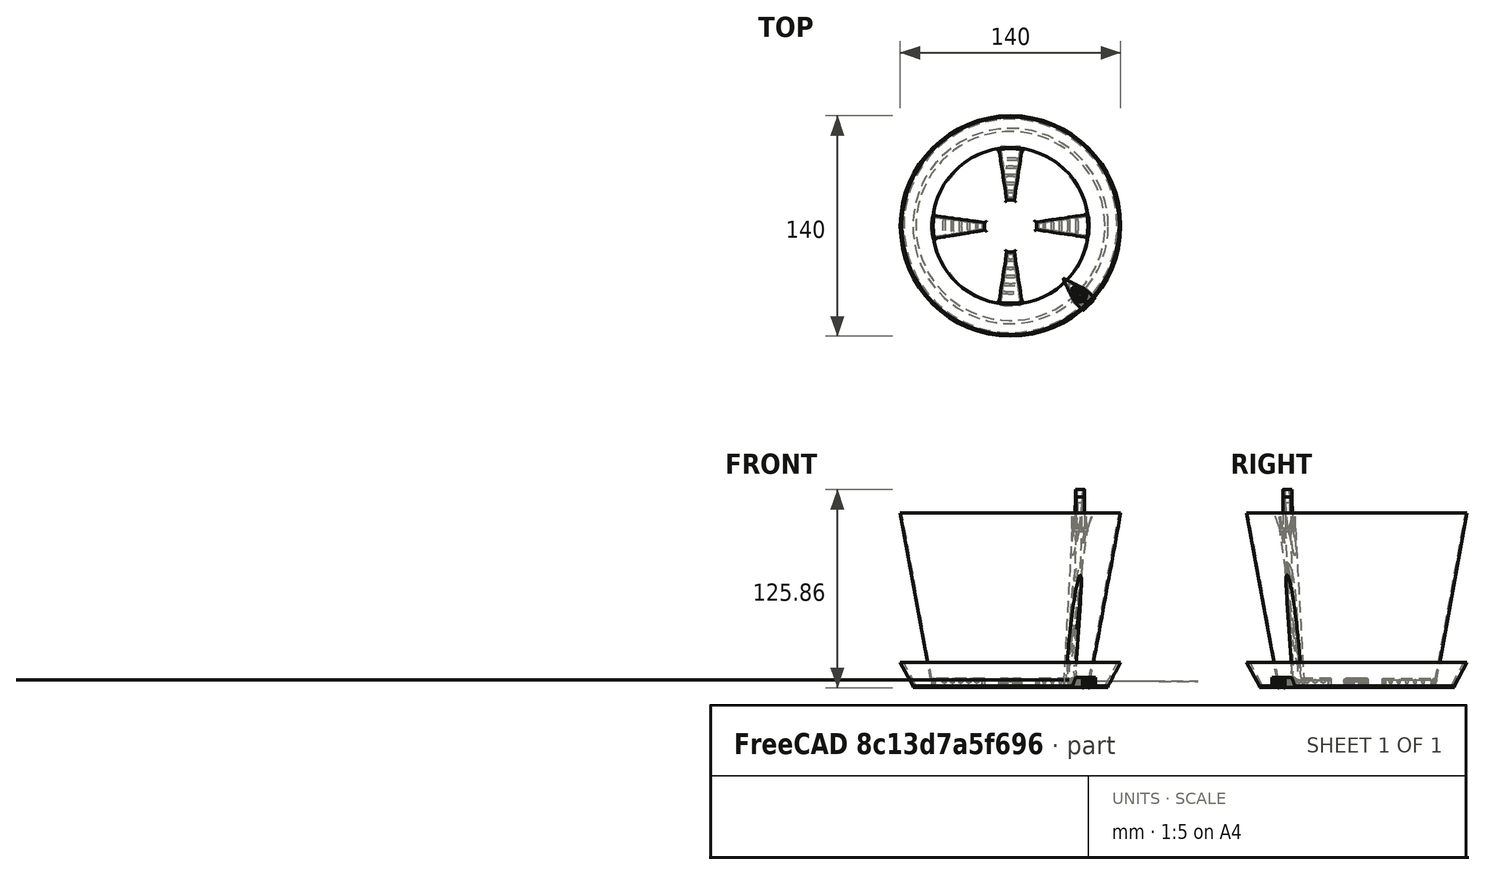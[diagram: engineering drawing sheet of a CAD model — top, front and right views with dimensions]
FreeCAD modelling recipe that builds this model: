
FCSTD DOCUMENT  (FreeCAD 0.19R19056 (Git))
Label: undervase3
License: All rights reserved
LicenseURL: http://en.wikipedia.org/wiki/All_rights_reserved
objects: Sketcher::SketchObject×32, PartDesign::Pad×9, PartDesign::AdditiveLoft×6, PartDesign::Pocket×6, PartDesign::Fillet×2, PartDesign::Body×2, PartDesign::SubtractivePipe×2, PartDesign::Chamfer×1, PartDesign::Thickness×1, PartDesign::AdditivePipe×1, PartDesign::Groove×1
note: 88 computed .brp shape members not serialized (recipe doc carries the construction recipe); baked Part::Feature solids carry a one-line shape summary decoded from their .brp

FEATURE [Sketcher::SketchObject] Sketch
  MapMode = 5
  Support = -> [XY_Plane]
  sketch-geometry (1):
    g0: Circle CenterX=0 CenterY=0 CenterZ=0 NormalX=0 NormalY=0 NormalZ=1 AngleXU=0 Radius=62
  constraints (2):
    c: Coincident(g0,g-1)
    c: Radius(g0) = 62
FEATURE [PartDesign::Pad] Pad
  Length = 1.6
  Length2 = 100
  Profile = -> Sketch
  Type = 0
FEATURE [Sketcher::SketchObject] Sketch001
  MapMode = 5
  Placement = pos=(0,0,1.6) rot=(0,0,1;0rad)
  Support = -> [Pad]
  sketch-geometry (2):
    g0: Circle CenterX=0 CenterY=0 CenterZ=0 NormalX=0 NormalY=0 NormalZ=1 AngleXU=0 Radius=60
    g1: Circle CenterX=0 CenterY=0 CenterZ=0 NormalX=0 NormalY=0 NormalZ=1 AngleXU=0 Radius=62
  constraints (4):
    c: Coincident(g0,g-1)
    c: Coincident(g1,g0)
    c: Radius(g0) = 60
    c: Radius(g1) = 62
FEATURE [Sketcher::SketchObject] Sketch002
  AttachmentOffset = pos=(0,0,15) rot=(0,0,1;0rad)
  MapMode = 5
  Placement = pos=(0,0,16.6) rot=(0,0,1;0rad)
  Support = -> [Pad]
  sketch-geometry (2):
    g0: Circle CenterX=0 CenterY=0 CenterZ=0 NormalX=0 NormalY=0 NormalZ=1 AngleXU=0 Radius=68
    g1: Circle CenterX=0 CenterY=0 CenterZ=0 NormalX=0 NormalY=0 NormalZ=1 AngleXU=0 Radius=70
  constraints (4):
    c: Coincident(g0,g-1)
    c: Coincident(g1,g0)
    c: Radius(g1) = 70
    c: Radius(g0) = 68
FEATURE [PartDesign::AdditiveLoft] AdditiveLoft
  BaseFeature = -> Pad
  Closed = false
  Profile = -> Sketch001
  Ruled = false
  Sections = -> [Sketch002]
FEATURE [PartDesign::Chamfer] Chamfer
  Base = -> AdditiveLoft [Edge6]
  BaseFeature = -> AdditiveLoft
  Size = 0.5
FEATURE [Sketcher::SketchObject] Sketch018
  MapMode = 5
  Placement = pos=(0,0,1.6) rot=(0,0,1;0rad)
  sketch-geometry (2):
    g0: Circle CenterX=0 CenterY=0 CenterZ=0 NormalX=0 NormalY=0 NormalZ=1 AngleXU=0 Radius=50
    g1: Circle CenterX=0 CenterY=0 CenterZ=0 NormalX=0 NormalY=0 NormalZ=1 AngleXU=0 Radius=49.1
  constraints (4):
    c: Coincident(g0,g-1)
    c: Radius(g0) = 50
    c: Coincident(g1,g0)
    c: Radius(g1) = 49.1
FEATURE [Sketcher::SketchObject] Sketch019
  AttachmentOffset = pos=(0,0,110) rot=(0,0,1;0rad)
  MapMode = 5
  Placement = pos=(0,0,111.6) rot=(0,0,1;0rad)
  sketch-geometry (2):
    g0: Circle CenterX=0 CenterY=0 CenterZ=0 NormalX=0 NormalY=0 NormalZ=1 AngleXU=0 Radius=70
    g1: Circle CenterX=0 CenterY=0 CenterZ=0 NormalX=0 NormalY=0 NormalZ=1 AngleXU=0 Radius=69.1
  constraints (4):
    c: Coincident(g0,g-1)
    c: Coincident(g1,g0)
    c: Radius(g1) = 69.1
    c: Radius(g0) = 70
FEATURE [PartDesign::AdditiveLoft] AdditiveLoft001
  BaseFeature = -> Chamfer
  Closed = false
  Profile = -> Sketch018
  Ruled = false
  Sections = -> [Sketch019]
FEATURE [Sketcher::SketchObject] Sketch021
  AttachmentOffset = pos=(0,0,-50) rot=(0,0,1;0rad)
  MapMode = 5
  Placement = pos=(0,0,51.6) rot=(1,0,0;3.14159rad)
  sketch-geometry (2):
    g0: Circle CenterX=0 CenterY=0 CenterZ=0 NormalX=0 NormalY=0 NormalZ=1 AngleXU=0 Radius=2
    g1: Circle CenterX=0 CenterY=0 CenterZ=0 NormalX=0 NormalY=0 NormalZ=1 AngleXU=0 Radius=3
  constraints (4):
    c: Coincident(g0,g-1)
    c: Coincident(g1,g0)
    c: Radius(g1) = 3
    c: Radius(g0) = 2
FEATURE [Sketcher::SketchObject] Sketch022
  AttachmentOffset = pos=(0,0,-100) rot=(0,0,1;0rad)
  MapMode = 5
  Placement = pos=(0,0,101.6) rot=(1,0,0;3.14159rad)
  sketch-geometry (2):
    g0: Circle CenterX=0 CenterY=0 CenterZ=0 NormalX=0 NormalY=0 NormalZ=1 AngleXU=0 Radius=2
    g1: Circle CenterX=0 CenterY=0 CenterZ=0 NormalX=0 NormalY=0 NormalZ=1 AngleXU=0 Radius=2.8
  constraints (4):
    c: Coincident(g0,g-1)
    c: Coincident(g1,g0)
    c: Radius(g0) = 2
    c: Radius(g1) = 2.8
FEATURE [PartDesign::AdditiveLoft] AdditiveLoft002
  BaseFeature = -> AdditiveLoft001
  Closed = false
  Profile = -> Sketch021
  Ruled = false
  Sections = -> [Sketch022]
FEATURE [Sketcher::SketchObject] Sketch026
  ExternalGeometry = -> [Sketch018]
  MapMode = 5
  Placement = pos=(0,0,1) rot=(1,0,0;3.14159rad)
  sketch-geometry (59):
    g0: LineSegment [constr] StartX=0 StartY=0 StartZ=0 EndX=-7.39047 EndY=-49.4508 EndZ=0
    g1: LineSegment [constr] StartX=7.39047 StartY=-49.4508 StartZ=0 EndX=-9e-16 EndY=0 EndZ=0
    g2: LineSegment [constr] StartX=49.4508 StartY=-7.39047 StartZ=0 EndX=0 EndY=0 EndZ=0
    g3: LineSegment [constr] StartX=49.4508 StartY=7.39047 StartZ=0 EndX=0 EndY=0 EndZ=0
    g4: LineSegment [constr] StartX=7.39047 StartY=49.4508 StartZ=0 EndX=9e-16 EndY=0 EndZ=0
    g5: LineSegment [constr] StartX=-7.39047 StartY=49.4508 StartZ=0 EndX=0 EndY=0 EndZ=0
    g6: Circle [constr] CenterX=0 CenterY=0 CenterZ=0 NormalX=0 NormalY=0 NormalZ=1 AngleXU=0 Radius=7
    g7: LineSegment [constr] StartX=-49.5634 StartY=-6.59349 StartZ=0 EndX=0 EndY=0 EndZ=0
    g8: LineSegment [constr] StartX=-49.3254 StartY=8.18553 StartZ=0 EndX=0 EndY=0 EndZ=0
    g9: LineSegment [constr] StartX=6.40003 StartY=-49.5887 StartZ=0 EndX=-9e-16 EndY=-6.92311 EndZ=0
    g10: LineSegment [constr] StartX=-6.40003 StartY=-49.5887 StartZ=0 EndX=-9e-16 EndY=-6.92311 EndZ=0
    g11: LineSegment [constr] StartX=49.5887 StartY=6.40003 StartZ=0 EndX=6.92311 EndY=0 EndZ=0
    g12: LineSegment [constr] StartX=49.5887 StartY=-6.40003 StartZ=0 EndX=6.92311 EndY=0 EndZ=0
    g13: LineSegment [constr] StartX=-6.40004 StartY=49.5887 StartZ=0 EndX=0 EndY=6.92311 EndZ=0
    g14: LineSegment [constr] StartX=6.40003 StartY=49.5887 StartZ=0 EndX=0 EndY=6.92311 EndZ=0
    g15: Circle [constr] CenterX=0 CenterY=0 CenterZ=0 NormalX=0 NormalY=0 NormalZ=1 AngleXU=0 Radius=16.5
    g16: LineSegment [constr] StartX=-49.4793 StartY=7.19744 StartZ=0 EndX=-6.92221 EndY=0.111443 EndZ=0
    g17: LineSegment [constr] StartX=-49.6853 StartY=-5.60096 StartZ=0 EndX=-6.92221 EndY=0.111443 EndZ=0
    g18: GeomPoint X=-1.03467 Y=6.92311 Z=0
    g19: GeomPoint X=1.03467 Y=6.92311 Z=0
    g20: GeomPoint X=6.92311 Y=1.03467 Z=0
    g21: GeomPoint X=6.92311 Y=-1.03467 Z=0
    g22: GeomPoint X=1.03467 Y=-6.92311 Z=0
    g23: GeomPoint X=-1.03467 Y=-6.92311 Z=0
    g24: GeomPoint X=-6.93887 Y=-0.923089 Z=0
    g25: GeomPoint X=-6.90556 Y=1.14597 Z=0
    g26: ArcOfCircle CenterX=0 CenterY=0 CenterZ=0 NormalX=0 NormalY=0 NormalZ=1 AngleXU=0 Radius=50 StartAngle=2.97714 EndAngle=2.99714
    g27: ArcOfCircle CenterX=0 CenterY=0 CenterZ=0 NormalX=0 NormalY=0 NormalZ=1 AngleXU=0 Radius=50 StartAngle=3.25385 EndAngle=3.27385
    g28: ArcOfCircle CenterX=0 CenterY=0 CenterZ=0 NormalX=0 NormalY=0 NormalZ=1 AngleXU=0 Radius=50 StartAngle=0.128353 EndAngle=0.148353
    g29: ArcOfCircle CenterX=0 CenterY=0 CenterZ=0 NormalX=0 NormalY=0 NormalZ=1 AngleXU=0 Radius=50 StartAngle=6.13483 EndAngle=6.15483
    g30: ArcOfCircle CenterX=0 CenterY=0 CenterZ=0 NormalX=0 NormalY=0 NormalZ=1 AngleXU=0 Radius=50 StartAngle=4.56404 EndAngle=4.58404
    g31: ArcOfCircle CenterX=0 CenterY=0 CenterZ=0 NormalX=0 NormalY=0 NormalZ=1 AngleXU=0 Radius=50 StartAngle=4.84074 EndAngle=4.86074
    g32: ArcOfCircle CenterX=0 CenterY=0 CenterZ=0 NormalX=0 NormalY=0 NormalZ=1 AngleXU=0 Radius=50 StartAngle=1.69915 EndAngle=1.71915
    g33: ArcOfCircle CenterX=0 CenterY=0 CenterZ=0 NormalX=0 NormalY=0 NormalZ=1 AngleXU=0 Radius=50 StartAngle=1.42244 EndAngle=1.44244
    g34: Circle [constr] CenterX=0 CenterY=0 CenterZ=0 NormalX=0 NormalY=0 NormalZ=1 AngleXU=0 Radius=18
    g35: LineSegment StartX=-49.3254 StartY=8.18553 StartZ=0 EndX=-16.2774 EndY=2.70123 EndZ=0
    g36: LineSegment StartX=-49.4793 StartY=7.19744 StartZ=0 EndX=-17.8953 EndY=1.93853 EndZ=0
    g37: LineSegment StartX=-49.6853 StartY=-5.60096 StartZ=0 EndX=-17.9484 EndY=-1.36147 EndZ=0
    g38: LineSegment StartX=-49.5634 StartY=-6.59349 StartZ=0 EndX=-16.3559 EndY=-2.17585 EndZ=0
    g39: LineSegment StartX=49.4508 StartY=7.39047 StartZ=0 EndX=16.3188 EndY=2.43886 EndZ=0
    g40: LineSegment StartX=49.5887 StartY=6.40003 StartZ=0 EndX=17.9242 EndY=1.65021 EndZ=0
    g41: LineSegment StartX=49.5887 StartY=-6.40003 StartZ=0 EndX=17.9242 EndY=-1.65021 EndZ=0
    g42: LineSegment StartX=49.4508 StartY=-7.39047 StartZ=0 EndX=16.3188 EndY=-2.43886 EndZ=0
    g43: ArcOfCircle CenterX=0 CenterY=0 CenterZ=0 NormalX=0 NormalY=0 NormalZ=1 AngleXU=0 Radius=18 StartAngle=3.03369 EndAngle=3.2173
    g44: ArcOfCircle CenterX=0 CenterY=0 CenterZ=0 NormalX=0 NormalY=0 NormalZ=1 AngleXU=0 Radius=16.5 StartAngle=2.97714 EndAngle=3.27385
    g45: ArcOfCircle CenterX=0 CenterY=0 CenterZ=0 NormalX=0 NormalY=0 NormalZ=1 AngleXU=0 Radius=18 StartAngle=6.19138 EndAngle=6.37499
    g46: ArcOfCircle CenterX=0 CenterY=0 CenterZ=0 NormalX=0 NormalY=0 NormalZ=1 AngleXU=0 Radius=16.5 StartAngle=6.13483 EndAngle=6.43154
    g47: LineSegment StartX=-7.39047 StartY=49.4508 StartZ=0 EndX=-2.43886 EndY=16.3188 EndZ=0
    g48: LineSegment StartX=-6.40004 StartY=49.5887 StartZ=0 EndX=-1.65022 EndY=17.9242 EndZ=0
    g49: LineSegment StartX=6.40003 StartY=49.5887 StartZ=0 EndX=1.65021 EndY=17.9242 EndZ=0
    g50: LineSegment StartX=7.39047 StartY=49.4508 StartZ=0 EndX=2.43886 EndY=16.3188 EndZ=0
    g51: ArcOfCircle CenterX=0 CenterY=0 CenterZ=0 NormalX=0 NormalY=0 NormalZ=1 AngleXU=0 Radius=16.5 StartAngle=1.42244 EndAngle=1.71915
    g52: ArcOfCircle CenterX=0 CenterY=0 CenterZ=0 NormalX=0 NormalY=0 NormalZ=1 AngleXU=0 Radius=18 StartAngle=1.47899 EndAngle=1.6626
    g53: LineSegment StartX=-7.39047 StartY=-49.4508 StartZ=0 EndX=-2.43886 EndY=-16.3188 EndZ=0
    g54: LineSegment StartX=-6.40003 StartY=-49.5887 StartZ=0 EndX=-1.65021 EndY=-17.9242 EndZ=0
    g55: LineSegment StartX=6.40003 StartY=-49.5887 StartZ=0 EndX=1.65021 EndY=-17.9242 EndZ=0
    g56: LineSegment StartX=7.39047 StartY=-49.4508 StartZ=0 EndX=2.43886 EndY=-16.3188 EndZ=0
    g57: ArcOfCircle CenterX=0 CenterY=0 CenterZ=0 NormalX=0 NormalY=0 NormalZ=1 AngleXU=0 Radius=16.5 StartAngle=4.56404 EndAngle=4.86074
    g58: ArcOfCircle CenterX=0 CenterY=0 CenterZ=0 NormalX=0 NormalY=0 NormalZ=1 AngleXU=0 Radius=18 StartAngle=4.62058 EndAngle=4.8042
  constraints (148):
    c: Coincident(g8,g7)
    c: Radius(g6) = 7
    c: Coincident(g10,g9)
    c: Coincident(g12,g11)
    c: Coincident(g14,g13)
    c: Radius(g15) = 16.5
    c: Coincident(g6,g-1)
    c: Coincident(g15,g-1)
    c: PointOnObject(g11,g-3)
    c: PointOnObject(g12,g-3)
    c: PointOnObject(g4,g-3)
    c: PointOnObject(g5,g-3)
    c: PointOnObject(g8,g-3)
    c: PointOnObject(g7,g-3)
    c: PointOnObject(g10,g-3)
    c: PointOnObject(g1,g-3)
    c: Coincident(g4,g-1)
    c: Coincident(g0,g-1)
    c: Coincident(g7,g1)
    c: Coincident(g7,g-1)
    c: Coincident(g2,g-1)
    c: Coincident(g3,g-1)
    c: Coincident(g5,g-1)
    c: Coincident(g17,g16)
    c: Angle(g8,g7) = 0.296706
    c: Angle(g4,g5) = 0.296706
    c: Angle(g2,g3) = 0.296706
    c: Angle(g0,g1) = 0.296706
    c: PointOnObject(g18,g6)
    c: PointOnObject(g19,g6)
    c: PointOnObject(g20,g6)
    c: PointOnObject(g21,g6)
    c: PointOnObject(g22,g6)
    c: PointOnObject(g24,g6)
    c: PointOnObject(g25,g6)
    c: PointOnObject(g25,g8)
    c: PointOnObject(g24,g7)
    c: PointOnObject(g23,g0)
    c: PointOnObject(g22,g1)
    c: PointOnObject(g21,g2)
    c: PointOnObject(g20,g3)
    c: PointOnObject(g19,g4)
    c: PointOnObject(g18,g5)
    c: PointOnObject(g23,g6)
    c: Symmetric(g23,g22,g9)
    c: Symmetric(g25,g24,g16)
    c: Symmetric(g18,g19,g13)
    c: Symmetric(g20,g21,g11)
    c: PointOnObject(g13,g-2)
    c: PointOnObject(g11,g-1)
    c: PointOnObject(g9,g-2)
    c: Distance(g0,g10) = 1
    c: Distance(g11,g3) = 1
    c: Distance(g4,g14) = 1
    c: Distance(g8,g16) = 1
    c: Distance(g17,g7) = 1
    c: Coincident(g26,g-1)
    c: Coincident(g26,g8)
    c: Coincident(g26,g16)
    c: Coincident(g27,g26)
    c: Coincident(g27,g17)
    c: Coincident(g27,g7)
    c: Coincident(g28,g26)
    c: Coincident(g28,g3)
    c: Coincident(g28,g11)
    c: Coincident(g29,g26)
    c: Coincident(g29,g12)
    c: Coincident(g29,g2)
    c: Distance(g29,g29) = 1
    c: Coincident(g30,g26)
    c: Coincident(g30,g0)
    c: Coincident(g30,g10)
    c: Coincident(g31,g26)
    c: Coincident(g31,g9)
    c: Coincident(g31,g1)
    c: Coincident(g32,g26)
    c: Coincident(g32,g5)
    c: Coincident(g32,g13)
    c: Coincident(g33,g26)
    c: Coincident(g33,g14)
    c: Coincident(g33,g4)
    c: Coincident(g34,g26)
    c: Radius(g34) = 18
    c: Coincident(g35,g26)
    c: PointOnObject(g35,g8)
    c: Coincident(g36,g26)
    c: PointOnObject(g36,g16)
    c: Coincident(g37,g27)
    c: PointOnObject(g37,g17)
    c: Coincident(g38,g27)
    c: PointOnObject(g38,g7)
    c: Coincident(g39,g28)
    c: PointOnObject(g39,g3)
    c: Coincident(g40,g28)
    c: PointOnObject(g40,g11)
    c: Coincident(g41,g29)
    c: PointOnObject(g41,g12)
    c: Coincident(g42,g29)
    c: PointOnObject(g42,g2)
    c: PointOnObject(g36,g34)
    c: PointOnObject(g35,g15)
    c: PointOnObject(g41,g34)
    c: PointOnObject(g39,g15)
    c: Coincident(g43,g26)
    c: Coincident(g43,g36)
    c: Coincident(g43,g37)
    c: Coincident(g44,g26)
    c: Coincident(g44,g35)
    c: Coincident(g44,g38)
    c: Coincident(g45,g26)
    c: Coincident(g45,g40)
    c: Coincident(g45,g41)
    c: Coincident(g46,g26)
    c: Coincident(g46,g39)
    c: Coincident(g46,g42)
    c: Coincident(g47,g32)
    c: PointOnObject(g47,g5)
    c: Coincident(g48,g32)
    c: PointOnObject(g48,g13)
    c: Coincident(g49,g33)
    c: PointOnObject(g49,g14)
    c: Coincident(g50,g33)
    c: PointOnObject(g50,g4)
    c: PointOnObject(g47,g15)
    c: PointOnObject(g49,g34)
    c: Coincident(g51,g26)
    c: Coincident(g51,g47)
    c: Coincident(g51,g50)
    c: Coincident(g52,g26)
    c: Coincident(g52,g48)
    c: Coincident(g52,g49)
    c: Coincident(g53,g30)
    c: PointOnObject(g53,g0)
    c: Coincident(g54,g30)
    c: PointOnObject(g54,g10)
    c: Coincident(g55,g31)
    c: PointOnObject(g55,g9)
    c: Coincident(g56,g31)
    c: PointOnObject(g56,g1)
    c: PointOnObject(g56,g15)
    c: PointOnObject(g54,g34)
    c: PointOnObject(g55,g34)
    c: Coincident(g57,g26)
    c: Coincident(g57,g53)
    c: Coincident(g57,g56)
    c: Coincident(g58,g26)
    c: Coincident(g58,g54)
    c: Coincident(g58,g55)
FEATURE [PartDesign::Pad] Pad017
  BaseFeature = -> AdditiveLoft002
  Length = 4
  Length2 = 100
  Profile = -> Sketch026
  Reversed = true
  Type = 0
FEATURE [Sketcher::SketchObject] Sketch027
  AttachmentOffset = pos=(0,0,51) rot=(0,0,1;0rad)
  ExternalGeometry = -> [Pad017]
  MapMode = 5
  Placement = pos=(0,-51,-5.2771e-12) rot=(1,0,0;1.5708rad)
  Support = -> [XZ_Plane]
  sketch-geometry (4):
    g0: LineSegment StartX=-6.35823 StartY=5 StartZ=0 EndX=6.26649 EndY=5 EndZ=0
    g1: LineSegment StartX=6.26649 StartY=5 StartZ=0 EndX=6.26649 EndY=1.6 EndZ=0
    g2: LineSegment StartX=6.26649 StartY=1.6 StartZ=0 EndX=-6.35823 EndY=1.6 EndZ=0
    g3: LineSegment StartX=-6.35823 StartY=1.6 StartZ=0 EndX=-6.35823 EndY=5 EndZ=0
  constraints (10):
    c: Coincident(g0,g1)
    c: Coincident(g1,g2)
    c: Coincident(g2,g3)
    c: Coincident(g3,g0)
    c: Horizontal(g0)
    c: Horizontal(g2)
    c: Vertical(g1)
    c: Vertical(g3)
    c: Coincident(g0,g-3)
    c: Coincident(g1,g-4)
FEATURE [PartDesign::Pocket] Pocket
  BaseFeature = -> Pad017
  Length = 4
  Length2 = 100
  Profile = -> Sketch027
  Type = 0
FEATURE [Sketcher::SketchObject] Sketch028
  AttachmentOffset = pos=(0,0,-50.5) rot=(0,0,1;0rad)
  ExternalGeometry = -> [Pocket]
  MapMode = 5
  Placement = pos=(0,50.5,5.2254e-12) rot=(1,0,0;1.5708rad)
  Support = -> [XZ_Plane]
  sketch-geometry (4):
    g0: LineSegment StartX=-6.35823 StartY=5 StartZ=0 EndX=6.26649 EndY=5 EndZ=0
    g1: LineSegment StartX=6.26649 StartY=5 StartZ=0 EndX=6.26649 EndY=1.6 EndZ=0
    g2: LineSegment StartX=6.26649 StartY=1.6 StartZ=0 EndX=-6.35823 EndY=1.6 EndZ=0
    g3: LineSegment StartX=-6.35823 StartY=1.6 StartZ=0 EndX=-6.35823 EndY=5 EndZ=0
  constraints (10):
    c: Coincident(g0,g1)
    c: Coincident(g1,g2)
    c: Coincident(g2,g3)
    c: Coincident(g3,g0)
    c: Horizontal(g0)
    c: Horizontal(g2)
    c: Vertical(g1)
    c: Vertical(g3)
    c: Coincident(g0,g-4)
    c: Coincident(g1,g-3)
FEATURE [PartDesign::Pocket] Pocket001
  BaseFeature = -> Pocket
  Length = 3
  Length2 = 100
  Profile = -> Sketch028
  Reversed = true
  Type = 0
FEATURE [Sketcher::SketchObject] Sketch029
  AttachmentOffset = pos=(0,0,50.5) rot=(0,0,1;0rad)
  ExternalGeometry = -> [Pocket001]
  MapMode = 5
  Placement = pos=(50.5,-5.7019e-12,5.7019e-12) rot=(0.57735,0.57735,0.57735;2.0944rad)
  Support = -> [YZ_Plane]
  sketch-geometry (4):
    g0: LineSegment StartX=-6.35821 StartY=5 StartZ=0 EndX=6.26649 EndY=5 EndZ=0
    g1: LineSegment StartX=6.26649 StartY=5 StartZ=0 EndX=6.26649 EndY=1.6 EndZ=0
    g2: LineSegment StartX=6.26649 StartY=1.6 StartZ=0 EndX=-6.35821 EndY=1.6 EndZ=0
    g3: LineSegment StartX=-6.35821 StartY=1.6 StartZ=0 EndX=-6.35821 EndY=5 EndZ=0
  constraints (10):
    c: Coincident(g0,g1)
    c: Coincident(g1,g2)
    c: Coincident(g2,g3)
    c: Coincident(g3,g0)
    c: Horizontal(g0)
    c: Horizontal(g2)
    c: Vertical(g1)
    c: Vertical(g3)
    c: Coincident(g0,g-3)
    c: Coincident(g1,g-4)
FEATURE [PartDesign::Pocket] Pocket002
  BaseFeature = -> Pocket001
  Length = 3
  Length2 = 100
  Profile = -> Sketch029
  Type = 0
FEATURE [Sketcher::SketchObject] Sketch030
  AttachmentOffset = pos=(0,0,-50.5) rot=(0,0,1;0rad)
  ExternalGeometry = -> [Pocket002]
  MapMode = 5
  Placement = pos=(-50.5,5.7019e-12,-5.7019e-12) rot=(0.57735,0.57735,0.57735;2.0944rad)
  Support = -> [YZ_Plane]
  sketch-geometry (4):
    g0: LineSegment StartX=-7.15114 StartY=5 StartZ=0 EndX=5.48177 EndY=5 EndZ=0
    g1: LineSegment StartX=5.48177 StartY=5 StartZ=0 EndX=5.48177 EndY=1.6 EndZ=0
    g2: LineSegment StartX=5.48177 StartY=1.6 StartZ=0 EndX=-7.15114 EndY=1.6 EndZ=0
    g3: LineSegment StartX=-7.15114 StartY=1.6 StartZ=0 EndX=-7.15114 EndY=5 EndZ=0
  constraints (10):
    c: Coincident(g0,g1)
    c: Coincident(g1,g2)
    c: Coincident(g2,g3)
    c: Coincident(g3,g0)
    c: Horizontal(g0)
    c: Horizontal(g2)
    c: Vertical(g1)
    c: Vertical(g3)
    c: Coincident(g0,g-4)
    c: Coincident(g1,g-3)
FEATURE [PartDesign::Pocket] Pocket003
  BaseFeature = -> Pocket002
  Length = 3
  Length2 = 100
  Profile = -> Sketch030
  Reversed = true
  Type = 0
FEATURE [Sketcher::SketchObject] Sketch031
  ExternalGeometry = -> [Pocket003,Sketch018,Sketch026]
  MapMode = 5
  Placement = pos=(0,0,5) rot=(0,0,1;0rad)
  Support = -> [Pocket003]
  sketch-geometry (16):
    g0: ArcOfCircle CenterX=0 CenterY=0 CenterZ=0 NormalX=0 NormalY=0 NormalZ=1 AngleXU=0 Radius=16.5 StartAngle=3.00934 EndAngle=3.30604
    g1: ArcOfCircle CenterX=0 CenterY=0 CenterZ=0 NormalX=0 NormalY=0 NormalZ=1 AngleXU=0 Radius=49.1 StartAngle=3.00934 EndAngle=3.30604
    g2: LineSegment StartX=-48.6712 StartY=6.47481 StartZ=0 EndX=-16.3559 EndY=2.17585 EndZ=0
    g3: LineSegment StartX=-16.2774 StartY=-2.70123 StartZ=0 EndX=-48.4376 EndY=-8.03819 EndZ=0
    g4: LineSegment StartX=-2.43886 StartY=-16.3188 StartZ=0 EndX=-7.33135 EndY=-48.5496 EndZ=0
    g5: LineSegment StartX=7.33136 StartY=-48.5496 StartZ=0 EndX=2.43886 EndY=-16.3188 EndZ=0
    g6: LineSegment StartX=48.5496 StartY=7.33134 StartZ=0 EndX=16.3188 EndY=2.43886 EndZ=0
    g7: LineSegment StartX=48.5496 StartY=-7.33134 StartZ=0 EndX=16.3188 EndY=-2.43886 EndZ=0
    g8: LineSegment StartX=-7.33133 StartY=48.5496 StartZ=0 EndX=-2.43886 EndY=16.3188 EndZ=0
    g9: LineSegment StartX=2.43886 StartY=16.3188 StartZ=0 EndX=7.33135 EndY=48.5496 EndZ=0
    g10: ArcOfCircle CenterX=0 CenterY=0 CenterZ=0 NormalX=0 NormalY=0 NormalZ=1 AngleXU=0 Radius=16.5 StartAngle=4.56404 EndAngle=4.86074
    g11: ArcOfCircle CenterX=0 CenterY=0 CenterZ=0 NormalX=0 NormalY=0 NormalZ=1 AngleXU=0 Radius=49.1 StartAngle=4.56251 EndAngle=4.86226
    g12: ArcOfCircle CenterX=0 CenterY=0 CenterZ=0 NormalX=0 NormalY=0 NormalZ=1 AngleXU=0 Radius=16.5 StartAngle=6.13483 EndAngle=6.43154
    g13: ArcOfCircle CenterX=0 CenterY=0 CenterZ=0 NormalX=0 NormalY=0 NormalZ=1 AngleXU=0 Radius=49.1 StartAngle=6.13331 EndAngle=6.43306
    g14: ArcOfCircle CenterX=0 CenterY=0 CenterZ=0 NormalX=0 NormalY=0 NormalZ=1 AngleXU=0 Radius=16.5 StartAngle=1.42244 EndAngle=1.71915
    g15: ArcOfCircle CenterX=0 CenterY=0 CenterZ=0 NormalX=0 NormalY=0 NormalZ=1 AngleXU=0 Radius=49.1 StartAngle=1.42092 EndAngle=1.72067
  constraints (37):
    c: Coincident(g0,g-1)
    c: Coincident(g0,g-5)
    c: Coincident(g0,g-6)
    c: Coincident(g1,g0)
    c: PointOnObject(g1,g-5)
    c: PointOnObject(g1,g-6)
    c: PointOnObject(g1,g-4)
    c: Coincident(g2,g1)
    c: Coincident(g2,g0)
    c: Coincident(g3,g0)
    c: Coincident(g3,g1)
    c: Coincident(g4,g-7)
    c: Coincident(g6,g-10)
    c: Coincident(g7,g-9)
    c: Coincident(g8,g-11)
    c: Coincident(g9,g-12)
    c: PointOnObject(g4,g-4)
    c: Coincident(g10,g0)
    c: Coincident(g10,g4)
    c: Coincident(g10,g5)
    c: Coincident(g11,g0)
    c: Coincident(g11,g4)
    c: Coincident(g11,g5)
    c: PointOnObject(g6,g-4)
    c: Coincident(g12,g0)
    c: Coincident(g12,g6)
    c: Coincident(g12,g7)
    c: Coincident(g13,g0)
    c: Coincident(g13,g6)
    c: Coincident(g13,g7)
    c: PointOnObject(g8,g-4)
    c: Coincident(g14,g0)
    c: Coincident(g14,g8)
    c: Coincident(g14,g9)
    c: Coincident(g15,g0)
    c: Coincident(g15,g8)
    c: Coincident(g15,g9)
FEATURE [PartDesign::Pad] Pad018
  BaseFeature = -> Pocket003
  Length = 1.2
  Length2 = 100
  Profile = -> Sketch031
  Type = 0
FEATURE [PartDesign::Fillet] Fillet
  Base = -> Pad018 [Edge309,Edge307,Edge314,Edge316,Edge325,Edge327,Edge320,Edge322]
  BaseFeature = -> Pad018
  Radius = 1
FEATURE [PartDesign::Fillet] Fillet001
  Base = -> Fillet [Edge55,Edge65,Face25,Edge42]
  BaseFeature = -> Fillet
  Radius = 1
FEATURE [Sketcher::SketchObject] Sketch032
  AttachmentOffset = pos=(0,0,-12) rot=(0,0,1;0rad)
  ExternalGeometry = -> [Fillet001]
  MapMode = 5
  Placement = pos=(0,0,99.6) rot=(0,0,1;0rad)
  Support = -> [Fillet001]
  sketch-geometry (3):
    g0: LineSegment [constr] StartX=0 StartY=0 StartZ=0 EndX=72.7942 EndY=-72.7942 EndZ=0
    g1: Circle CenterX=44.0889 CenterY=-44.0889 CenterZ=0 NormalX=0 NormalY=0 NormalZ=1 AngleXU=0 Radius=5
    g2: GeomPoint X=49.4975 Y=-49.4975 Z=0
  constraints (4):
    c: Coincident(g0,g-1)
    c: Angle(g0,g-1) = 0.785398
    c: PointOnObject(g1,g0)
    c: Radius(g1) = 5
FEATURE [PartDesign::Pad] Pad019
  BaseFeature = -> Fillet001
  Length = 2
  Length2 = 100
  Profile = -> Sketch032
  Type = 0
FEATURE [Sketcher::SketchObject] Sketch033
  ExternalGeometry = -> [Pad019]
  MapMode = 5
  Placement = pos=(0,0,101.6) rot=(0,0,1;0rad)
  Support = -> [Pad019]
  sketch-geometry (2):
    g0: Circle CenterX=44.0889 CenterY=-44.0889 CenterZ=0 NormalX=0 NormalY=0 NormalZ=1 AngleXU=0 Radius=5
    g1: Circle CenterX=44.0889 CenterY=-44.0889 CenterZ=0 NormalX=0 NormalY=0 NormalZ=1 AngleXU=0 Radius=4
  constraints (4):
    c: Coincident(g0,g-3)
    c: Coincident(g1,g0)
    c: Equal(g0,g-3)
    c: Diameter(g1) = 8
FEATURE [Sketcher::SketchObject] Sketch034
  AttachmentOffset = pos=(0,0,10) rot=(0,0,1;0rad)
  ExternalGeometry = -> [Sketch033,Pad019]
  MapMode = 5
  Placement = pos=(0,0,111.6) rot=(0,0,1;0rad)
  Support = -> [Pad019]
  sketch-geometry (9):
    g0: LineSegment [constr] StartX=0 StartY=0 StartZ=0 EndX=52.6219 EndY=-44.7855 EndZ=0
    g1: LineSegment [constr] StartX=0 StartY=0 StartZ=0 EndX=44.7855 EndY=-52.6219 EndZ=0
    g2: GeomPoint X=40.2812 Y=-47.3295 Z=0
    g3: GeomPoint X=47.3295 Y=-40.2812 Z=0
    g4: ArcOfCircle CenterX=44.0889 CenterY=-44.0889 CenterZ=0 NormalX=0 NormalY=0 NormalZ=1 AngleXU=0 Radius=5 StartAngle=0.865679 EndAngle=3.84671
    g5: Circle CenterX=44.0889 CenterY=-44.0889 CenterZ=0 NormalX=0 NormalY=0 NormalZ=1 AngleXU=0 Radius=4.15
    g6: ArcOfCircle CenterX=0 CenterY=0 CenterZ=0 NormalX=0 NormalY=0 NormalZ=1 AngleXU=0 Radius=69.1 StartAngle=5.41751 EndAngle=5.57806
    g7: LineSegment StartX=40.2812 StartY=-47.3295 StartZ=0 EndX=44.7855 EndY=-52.6219 EndZ=0
    g8: LineSegment StartX=47.3295 StartY=-40.2812 StartZ=0 EndX=52.6219 EndY=-44.7855 EndZ=0
  constraints (20):
    c: Coincident(g0,g-1)
    c: PointOnObject(g0,g-4)
    c: Coincident(g1,g-1)
    c: PointOnObject(g2,g1)
    c: PointOnObject(g3,g0)
    c: Coincident(g4,g-3)
    c: Equal(g4,g-3)
    c: Coincident(g5,g4)
    c: Diameter(g5) = 8.3
    c: Tangent(g4,g0)
    c: Tangent(g1,g4)
    c: Coincident(g6,g-1)
    c: Coincident(g6,g0)
    c: Coincident(g6,g1)
    c: Coincident(g7,g2)
    c: Coincident(g7,g6)
    c: Coincident(g8,g3)
    c: Coincident(g8,g6)
    c: Coincident(g2,g4)
    c: Coincident(g4,g3)
FEATURE [PartDesign::AdditiveLoft] AdditiveLoft003
  BaseFeature = -> Pad019
  Closed = false
  Profile = -> Sketch033
  Ruled = false
  Sections = -> [Sketch034]
FEATURE [Sketcher::SketchObject] Sketch035
  ExternalGeometry = -> [AdditiveLoft003]
  MapMode = 5
  Placement = pos=(0,0,101.6) rot=(0,0,1;0rad)
  Support = -> [AdditiveLoft003]
  sketch-geometry (1):
    g0: Circle CenterX=44.0889 CenterY=-44.0889 CenterZ=0 NormalX=0 NormalY=0 NormalZ=1 AngleXU=0 Radius=3
  constraints (2):
    c: Coincident(g0,g-3)
    c: Diameter(g0) = 6
FEATURE [Sketcher::SketchObject] Sketch036
  AttachmentOffset = pos=(0,0,20) rot=(0,0,1;0rad)
  ExternalGeometry = -> [AdditiveLoft003]
  MapMode = 5
  Placement = pos=(0,0,121.6) rot=(0,0,1;0rad)
  Support = -> [AdditiveLoft003]
  sketch-geometry (1):
    g0: Circle CenterX=44.0889 CenterY=-44.0889 CenterZ=0 NormalX=0 NormalY=0 NormalZ=1 AngleXU=0 Radius=2.85
  constraints (2):
    c: Coincident(g0,g-3)
    c: Diameter(g0) = 5.7
FEATURE [PartDesign::AdditiveLoft] AdditiveLoft004
  BaseFeature = -> AdditiveLoft003
  Closed = false
  Profile = -> Sketch036
  Ruled = false
  Sections = -> [Sketch035]
FEATURE [Sketcher::SketchObject] Sketch037
  ExternalGeometry = -> [Pad019]
  MapMode = 5
  Placement = pos=(0,0,101.6) rot=(0,0,1;0rad)
  Support = -> [Pad019]
  sketch-geometry (1):
    g0: Circle CenterX=44.0889 CenterY=-44.0889 CenterZ=0 NormalX=0 NormalY=0 NormalZ=1 AngleXU=0 Radius=5
  constraints (2):
    c: Coincident(g0,g-3)
    c: Equal(g0,g-3)
FEATURE [Sketcher::SketchObject] Sketch038
  MapMode = 5
  Placement = pos=(0,0,1.6) rot=(0,0,1;0rad)
  Support = -> [Pad019]
  sketch-geometry (2):
    g0: LineSegment [constr] StartX=0 StartY=0 StartZ=0 EndX=33.9927 EndY=-33.9927 EndZ=0
    g1: Circle CenterX=33.9927 CenterY=-33.9927 CenterZ=0 NormalX=0 NormalY=0 NormalZ=1 AngleXU=0 Radius=0.5
  constraints (4):
    c: Coincident(g0,g-1)
    c: Angle(g0,g-1) = 0.785398
    c: Coincident(g1,g0)
    c: Diameter(g1) = 1
FEATURE [PartDesign::AdditiveLoft] AdditiveLoft005
  BaseFeature = -> AdditiveLoft004
  Closed = false
  Profile = -> Sketch038
  Ruled = false
  Sections = -> [Sketch037]
FEATURE [Sketcher::SketchObject] Sketch040
  AttachmentOffset = pos=(0,0,0) rot=(0,1,0;0.785398rad)
  MapMode = 5
  Placement = pos=(0,0,0) rot=(0.281085,0.678598,0.678598;2.59356rad)
  Support = -> [YZ_Plane]
  sketch-geometry (10):
    g0: Circle [constr] CenterX=-56.4164 CenterY=8.50651 CenterZ=0 NormalX=0 NormalY=0 NormalZ=1 AngleXU=0 Radius=2
    g1: Circle [constr] CenterX=-57.9319 CenterY=7.20143 CenterZ=0 NormalX=0 NormalY=0 NormalZ=1 AngleXU=0 Radius=2
    g2-g5: Circle [constr] x4 (B-spline internal-alignment scaffolding for g6; pole/knot coordinates omitted)
    g6: BSplineCurve PolesCount=4 KnotsCount=2 Degree=3 IsPeriodic=0
    g7: GeomPoint [constr] X=-62.6844 Y=2.96725 Z=0
    g8: GeomPoint [constr] X=-62.6568 Y=126.25 Z=0
    g9: LineSegment [constr] StartX=-65.2439 StartY=121.524 StartZ=0 EndX=-59.5808 EndY=121.54 EndZ=0
  constraints (10):
    c: Radius(g0) = 2
    c: Equal(g0,g1)
    c: PointOnObject(g1,g0)
    c: Radius(g2) = 2
    c: Equal(g2,g3)
    c: Equal(g2,g4)
    c: Equal(g2,g5)
    c: InternalAlignment(g2-g5 -> g6) x4
    c: InternalAlignment(g7,g6)
    c: InternalAlignment(g8,g6)
FEATURE [Sketcher::SketchObject] Sketch042
  MapMode = 5
  Support = -> [XY_Plane001]
  sketch-geometry (12):
    g0: LineSegment StartX=0 StartY=0 StartZ=0 EndX=6.5 EndY=0 EndZ=0
    g1: LineSegment [constr] StartX=-0.5 StartY=-1 StartZ=0 EndX=7 EndY=-1 EndZ=0
    g2: LineSegment StartX=0.5 StartY=-2.6 StartZ=0 EndX=6 EndY=-2.6 EndZ=0
    g3: LineSegment StartX=0 StartY=0 StartZ=0 EndX=-0.5 EndY=-1 EndZ=0
    g4: LineSegment StartX=-0.5 StartY=-1 StartZ=0 EndX=0.5 EndY=-2.6 EndZ=0
    g5: LineSegment StartX=6 StartY=-2.6 StartZ=0 EndX=7 EndY=-1 EndZ=0
    g6: LineSegment StartX=7 StartY=-1 StartZ=0 EndX=6.5 EndY=0 EndZ=0
    g7: GeomPoint X=0 Y=0 Z=0
    g8: LineSegment [constr] StartX=0 StartY=0 StartZ=0 EndX=0 EndY=-4.23763 EndZ=0
    g9: LineSegment [constr] StartX=6.5 StartY=0 StartZ=0 EndX=6.5 EndY=-3.6855 EndZ=0
    g10: LineSegment [constr] StartX=6 StartY=-2.6 StartZ=0 EndX=6.5 EndY=-2.6 EndZ=0
    g11: LineSegment [constr] StartX=0.5 StartY=-2.6 StartZ=0 EndX=0 EndY=-2.6 EndZ=0
  constraints (31):
    c: Coincident(g0,g-1)
    c: PointOnObject(g0,g-1)
    c: DistanceX(g0,g0) = 6.5
    c: Horizontal(g1)
    c: DistanceX(g1,g1) = 7.5
    c: DistanceY(g1,g-1) = 1
    c: Horizontal(g2)
    c: DistanceX(g2,g2) = 5.5
    c: DistanceY(g2,g-1) = 2.6
    c: Coincident(g3,g-1)
    c: Coincident(g3,g1)
    c: Coincident(g4,g1)
    c: Coincident(g4,g2)
    c: Coincident(g5,g2)
    c: Coincident(g5,g1)
    c: Coincident(g6,g1)
    c: Coincident(g6,g0)
    c: PointOnObject(g7,g0)
    c: Coincident(g8,g7)
    c: Vertical(g8)
    c: PointOnObject(g7,g3)
    c: Coincident(g9,g0)
    c: Vertical(g9)
    c: Coincident(g10,g2)
    c: PointOnObject(g10,g9)
    c: Horizontal(g10)
    c: Coincident(g11,g2)
    c: Horizontal(g11)
    c: Equal(g11,g10)
    c: Equal(g3,g6)
    c: Equal(g5,g4)
FEATURE [PartDesign::Pad] Pad020
  Length = 6
  Length2 = 100
  Profile = -> Sketch042
  Type = 0
FEATURE [PartDesign::Thickness] Thickness
  Base = -> Pad020 [Face8]
  BaseFeature = -> Pad020
  Intersection = false
  Join = 0
  Mode = 0
  Reversed = true
  Value = 0.2
FEATURE [Sketcher::SketchObject] Sketch043
  ExternalGeometry = -> [Thickness]
  MapMode = 5
  Placement = pos=(0,-2.6,0) rot=(1,0,0;1.5708rad)
  Support = -> [Thickness]
  sketch-geometry (8):
    g0: LineSegment StartX=5.9 StartY=3.5 StartZ=0 EndX=6 EndY=3.5 EndZ=0
    g1: LineSegment StartX=6 StartY=3.5 StartZ=0 EndX=6 EndY=2.5 EndZ=0
    g2: LineSegment StartX=6 StartY=2.5 StartZ=0 EndX=5.9 EndY=2.5 EndZ=0
    g3: LineSegment StartX=5.9 StartY=2.5 StartZ=0 EndX=5.9 EndY=3.5 EndZ=0
    g4: LineSegment StartX=0.5 StartY=3.5 StartZ=0 EndX=0.6 EndY=3.5 EndZ=0
    g5: LineSegment StartX=0.6 StartY=3.5 StartZ=0 EndX=0.6 EndY=2.5 EndZ=0
    g6: LineSegment StartX=0.6 StartY=2.5 StartZ=0 EndX=0.5 EndY=2.5 EndZ=0
    g7: LineSegment StartX=0.5 StartY=2.5 StartZ=0 EndX=0.5 EndY=3.5 EndZ=0
  constraints (24):
    c: Coincident(g0,g1)
    c: Coincident(g1,g2)
    c: Coincident(g2,g3)
    c: Coincident(g3,g0)
    c: Horizontal(g0)
    c: Horizontal(g2)
    c: Vertical(g1)
    c: Vertical(g3)
    c: Coincident(g4,g5)
    c: Coincident(g5,g6)
    c: Coincident(g6,g7)
    c: Coincident(g7,g4)
    c: Horizontal(g4)
    c: Horizontal(g6)
    c: Vertical(g5)
    c: Vertical(g7)
    c: PointOnObject(g0,g-4)
    c: PointOnObject(g4,g-5)
    c: DistanceY(g4,g-5) = 2.5
    c: DistanceY(g0,g-4) = 2.5
    c: DistanceY(g5,g5) = 1
    c: DistanceY(g3,g3) = 1
    c: DistanceX(g2,g2) = 0.1
    c: Equal(g2,g6)
FEATURE [PartDesign::Pad] Pad001
  BaseFeature = -> Thickness
  Length = 1
  Length2 = 100
  Profile = -> Sketch043
  Type = 0
FEATURE [Sketcher::SketchObject] Sketch044
  ExternalGeometry = -> [Pad001]
  MapMode = 5
  Placement = pos=(0,-2.6,0) rot=(1,0,0;1.5708rad)
  Support = -> [Pad001]
  sketch-geometry (10):
    g0: LineSegment StartX=1.1 StartY=0.5 StartZ=0 EndX=1.6 EndY=0.5 EndZ=0
    g1: LineSegment StartX=1.6 StartY=0.5 StartZ=0 EndX=1.6 EndY=0 EndZ=0
    g2: LineSegment StartX=1.6 StartY=0 StartZ=0 EndX=1.1 EndY=0 EndZ=0
    g3: LineSegment StartX=1.1 StartY=0 StartZ=0 EndX=1.1 EndY=0.5 EndZ=0
    g4: LineSegment StartX=4.9 StartY=0.5 StartZ=0 EndX=5.4 EndY=0.5 EndZ=0
    g5: LineSegment StartX=5.4 StartY=0.5 StartZ=0 EndX=5.4 EndY=0 EndZ=0
    g6: LineSegment StartX=5.4 StartY=0 StartZ=0 EndX=4.9 EndY=0 EndZ=0
    g7: LineSegment StartX=4.9 StartY=0 StartZ=0 EndX=4.9 EndY=0.5 EndZ=0
    g8: LineSegment [constr] StartX=5.4 StartY=0 StartZ=0 EndX=6 EndY=0 EndZ=0
    g9: LineSegment [constr] StartX=1.1 StartY=0 StartZ=0 EndX=0.5 EndY=0 EndZ=0
  constraints (30):
    c: Coincident(g0,g1)
    c: Coincident(g1,g2)
    c: Coincident(g2,g3)
    c: Coincident(g3,g0)
    c: Horizontal(g0)
    c: Horizontal(g2)
    c: Vertical(g1)
    c: Vertical(g3)
    c: Coincident(g4,g5)
    c: Coincident(g5,g6)
    c: Coincident(g6,g7)
    c: Coincident(g7,g4)
    c: Horizontal(g4)
    c: Horizontal(g6)
    c: Vertical(g5)
    c: Vertical(g7)
    c: DistanceX(g0,g4) = 3.3
    c: DistanceX(g4,g4) = 0.5
    c: DistanceY(g5,g5) = 0.5
    c: Equal(g5,g1)
    c: Equal(g0,g4)
    c: Coincident(g8,g5)
    c: PointOnObject(g8,g-3)
    c: Coincident(g9,g2)
    c: PointOnObject(g9,g-4)
    c: Horizontal(g8)
    c: Horizontal(g9)
    c: Equal(g8,g9)
    c: PointOnObject(g1,g-1)
    c: PointOnObject(g5,g-1)
FEATURE [PartDesign::Pad] Pad002
  BaseFeature = -> Pad001
  Length = 0.4
  Length2 = 100
  Profile = -> Sketch044
  Type = 0
FEATURE [Sketcher::SketchObject] Sketch003
  ExternalGeometry = -> [Pad002]
  MapMode = 5
  Placement = pos=(0,-2.6,0) rot=(1,0,0;1.5708rad)
  Support = -> [Pad002]
  sketch-geometry (26):
    g0: LineSegment StartX=1.65 StartY=0.65 StartZ=0 EndX=1.97 EndY=0.65 EndZ=0
    g1: LineSegment StartX=1.97 StartY=0.65 StartZ=0 EndX=1.97 EndY=-0.7 EndZ=0
    g2: LineSegment StartX=1.97 StartY=-0.7 StartZ=0 EndX=1.65 EndY=-0.7 EndZ=0
    g3: LineSegment StartX=1.65 StartY=-0.7 StartZ=0 EndX=1.65 EndY=0.65 EndZ=0
    g4: LineSegment StartX=2.37 StartY=0.65 StartZ=0 EndX=2.69 EndY=0.65 EndZ=0
    g5: LineSegment StartX=2.69 StartY=0.65 StartZ=0 EndX=2.69 EndY=-0.7 EndZ=0
    g6: LineSegment StartX=2.69 StartY=-0.7 StartZ=0 EndX=2.37 EndY=-0.7 EndZ=0
    g7: LineSegment StartX=2.37 StartY=-0.7 StartZ=0 EndX=2.37 EndY=0.65 EndZ=0
    g8: LineSegment StartX=3.09 StartY=0.65 StartZ=0 EndX=3.41 EndY=0.65 EndZ=0
    g9: LineSegment StartX=3.41 StartY=0.65 StartZ=0 EndX=3.41 EndY=-0.7 EndZ=0
    g10: LineSegment StartX=3.41 StartY=-0.7 StartZ=0 EndX=3.09 EndY=-0.7 EndZ=0
    g11: LineSegment StartX=3.09 StartY=-0.7 StartZ=0 EndX=3.09 EndY=0.65 EndZ=0
    g12: LineSegment StartX=3.81 StartY=0.65 StartZ=0 EndX=4.13 EndY=0.65 EndZ=0
    g13: LineSegment StartX=4.13 StartY=0.65 StartZ=0 EndX=4.13 EndY=-0.7 EndZ=0
    g14: LineSegment StartX=4.13 StartY=-0.7 StartZ=0 EndX=3.81 EndY=-0.7 EndZ=0
    g15: LineSegment StartX=3.81 StartY=-0.7 StartZ=0 EndX=3.81 EndY=0.65 EndZ=0
    g16: LineSegment StartX=4.53 StartY=0.65 StartZ=0 EndX=4.85 EndY=0.65 EndZ=0
    g17: LineSegment StartX=4.85 StartY=0.65 StartZ=0 EndX=4.85 EndY=-0.7 EndZ=0
    g18: LineSegment StartX=4.85 StartY=-0.7 StartZ=0 EndX=4.53 EndY=-0.7 EndZ=0
    g19: LineSegment StartX=4.53 StartY=-0.7 StartZ=0 EndX=4.53 EndY=0.65 EndZ=0
    g20: LineSegment [constr] StartX=1.97 StartY=0.65 StartZ=0 EndX=2.37 EndY=0.65 EndZ=0
    g21: LineSegment [constr] StartX=2.69 StartY=0.65 StartZ=0 EndX=3.09 EndY=0.65 EndZ=0
    g22: LineSegment [constr] StartX=3.41 StartY=0.65 StartZ=0 EndX=3.81 EndY=0.65 EndZ=0
    g23: LineSegment [constr] StartX=4.13 StartY=0.65 StartZ=0 EndX=4.53 EndY=0.65 EndZ=0
    g24: LineSegment [constr] StartX=1.65 StartY=0.65 StartZ=0 EndX=0.5 EndY=0.65 EndZ=0
    g25: LineSegment [constr] StartX=4.85 StartY=0.65 StartZ=0 EndX=6 EndY=0.65 EndZ=0
  constraints (74):
    c: Coincident(g0,g1)
    c: Coincident(g1,g2)
    c: Coincident(g2,g3)
    c: Coincident(g3,g0)
    c: Horizontal(g0)
    c: Horizontal(g2)
    c: Vertical(g1)
    c: Vertical(g3)
    c: Coincident(g4,g5)
    c: Coincident(g5,g6)
    c: Coincident(g6,g7)
    c: Coincident(g7,g4)
    c: Horizontal(g4)
    c: Horizontal(g6)
    c: Vertical(g5)
    c: Vertical(g7)
    c: Coincident(g8,g9)
    c: Coincident(g9,g10)
    c: Coincident(g10,g11)
    c: Coincident(g11,g8)
    c: Horizontal(g8)
    c: Horizontal(g10)
    c: Vertical(g9)
    c: Vertical(g11)
    c: Coincident(g12,g13)
    c: Coincident(g13,g14)
    c: Coincident(g14,g15)
    c: Coincident(g15,g12)
    c: Horizontal(g12)
    c: Horizontal(g14)
    c: Vertical(g13)
    c: Vertical(g15)
    c: Coincident(g16,g17)
    c: Coincident(g17,g18)
    c: Coincident(g18,g19)
    c: Coincident(g19,g16)
    c: Horizontal(g16)
    c: Horizontal(g18)
    c: Vertical(g17)
    c: Vertical(g19)
    c: DistanceX(g0,g0) = 0.32
    c: Equal(g0,g4)
    c: Equal(g4,g8)
    c: Equal(g8,g12)
    c: Equal(g12,g16)
    c: Equal(g17,g13)
    c: Equal(g13,g9)
    c: Equal(g9,g5)
    c: Equal(g5,g1)
    c: Coincident(g20,g0)
    c: Coincident(g20,g4)
    c: Coincident(g21,g4)
    c: Coincident(g21,g8)
    c: Coincident(g22,g8)
    c: Coincident(g23,g12)
    c: Coincident(g23,g16)
    c: Horizontal(g20)
    c: Horizontal(g21)
    c: Horizontal(g22)
    c: Horizontal(g23)
    c: Coincident(g22,g12)
    c: DistanceX(g2,g17) = 3.2
    c: Equal(g20,g21)
    c: Equal(g21,g22)
    c: Equal(g22,g23)
    c: Coincident(g24,g0)
    c: PointOnObject(g24,g-3)
    c: Horizontal(g24)
    c: Coincident(g25,g16)
    c: PointOnObject(g25,g-4)
    c: Horizontal(g25)
    c: Equal(g25,g24)
    c: DistanceY(g17,g17) = 1.35
    c: DistanceY(g17,g-4) = 0.7
FEATURE [PartDesign::Pad] Pad003
  BaseFeature = -> Pad002
  Length = 0.1
  Length2 = 100
  Profile = -> Sketch003
  Type = 0
FEATURE [PartDesign::Body] Body001  label="USB"
  Group = -> [Sketch042,Pad020,Thickness,Sketch043,Pad001,Sketch044,Pad002,Sketch003,Pad003]
  Origin = -> Origin001
  Placement = pos=(43.4641,-48.0298,4) rot=(0.862856,0.357407,0.357407;1.71777rad)
  Tip = -> Pad003
FEATURE [Sketcher::SketchObject] Sketch045
  ExternalGeometry = -> [AdditiveLoft005]
  MapMode = 5
  Placement = pos=(0,0,121.6) rot=(0,0,1;0rad)
  Support = -> [AdditiveLoft005]
  sketch-geometry (1):
    g0: Circle CenterX=44.0889 CenterY=-44.0889 CenterZ=0 NormalX=0 NormalY=0 NormalZ=1 AngleXU=0 Radius=2.85
  constraints (2):
    c: Coincident(g0,g-3)
    c: Equal(g0,g-3)
FEATURE [PartDesign::AdditivePipe] AdditivePipe
  AuxilleryCurvelinear = true
  AuxillerySpineTangent = false
  BaseFeature = -> AdditiveLoft005
  Binormal = (0,0,0)
  Mode = 0
  Profile = -> Sketch045
  Spine = -> Sketch040
  SpineTangent = false
  Transformation = 0
  Transition = 0
FEATURE [Sketcher::SketchObject] Sketch046
  ExternalGeometry = -> [AdditivePipe]
  MapMode = 5
  Placement = pos=(-0.230749,0.230749,126.087) rot=(-0.707107,-0.707106,0.000647;0.002588rad)
  Support = -> [AdditivePipe]
  sketch-geometry (1):
    g0: Circle CenterX=44.4198 CenterY=-44.42 CenterZ=0 NormalX=0 NormalY=0 NormalZ=1 AngleXU=0 Radius=1.5
  constraints (2):
    c: Coincident(g0,g-3)
    c: Diameter(g0) = 3
FEATURE [PartDesign::SubtractivePipe] SubtractivePipe
  AuxilleryCurvelinear = true
  AuxillerySpineTangent = false
  BaseFeature = -> AdditivePipe
  Binormal = (0,0,0)
  Mode = 0
  Profile = -> Sketch046
  Spine = -> Sketch040
  SpineTangent = false
  Transformation = 0
  Transition = 0
FEATURE [Sketcher::SketchObject] Sketch047
  AttachmentOffset = pos=(-43.5,0,43.5) rot=(0,1,0;-0.785398rad)
  MapMode = 5
  Placement = pos=(43.5,-43.5,9.8231e-12) rot=(-0.862856,-0.357407,-0.357407;4.56541rad)
  Support = -> [YZ_Plane]
  sketch-geometry (4):
    g0: LineSegment StartX=-6 StartY=7 StartZ=0 EndX=6 EndY=7 EndZ=0
    g1: LineSegment StartX=6 StartY=7 StartZ=0 EndX=6 EndY=0 EndZ=0
    g2: LineSegment StartX=6 StartY=0 StartZ=0 EndX=-6 EndY=0 EndZ=0
    g3: LineSegment StartX=-6 StartY=0 StartZ=0 EndX=-6 EndY=7 EndZ=0
  constraints (11):
    c: Coincident(g0,g1)
    c: Coincident(g1,g2)
    c: Coincident(g2,g3)
    c: Coincident(g3,g0)
    c: Horizontal(g0)
    c: Horizontal(g2)
    c: Vertical(g1)
    c: Vertical(g3)
    c: DistanceX(g0,g0) = 12
    c: DistanceY(g3,g3) = 7
    c: Symmetric(g1,g2,g-1)
FEATURE [PartDesign::Pad] Pad021
  BaseFeature = -> SubtractivePipe
  Length = 9
  Length2 = 100
  Profile = -> Sketch047
  Type = 0
FEATURE [Sketcher::SketchObject] Sketch048
  ExternalGeometry = -> [Pad021]
  MapMode = 5
  Placement = pos=(49.864,-49.864,1.12639e-11) rot=(0.862856,0.357407,0.357407;1.71777rad)
  Support = -> [Pad021]
  sketch-geometry (4):
    g0: LineSegment StartX=-4.5 StartY=5.5 StartZ=0 EndX=4.5 EndY=5.5 EndZ=0
    g1: LineSegment StartX=4.5 StartY=5.5 StartZ=0 EndX=4.5 EndY=1 EndZ=0
    g2: LineSegment StartX=4.5 StartY=1 StartZ=0 EndX=-4.5 EndY=1 EndZ=0
    g3: LineSegment StartX=-4.5 StartY=1 StartZ=0 EndX=-4.5 EndY=5.5 EndZ=0
  constraints (12):
    c: Coincident(g0,g1)
    c: Coincident(g1,g2)
    c: Coincident(g2,g3)
    c: Coincident(g3,g0)
    c: Horizontal(g0)
    c: Horizontal(g2)
    c: Vertical(g1)
    c: Vertical(g3)
    c: DistanceX(g0,g-4) = 1.5
    c: DistanceX(g-3,g0) = 1.5
    c: DistanceY(g0,g-4) = 1.5
    c: DistanceY(g-4,g1) = 1
FEATURE [PartDesign::Pocket] Pocket004
  BaseFeature = -> Pad021
  Length = 9
  Length2 = 100
  Profile = -> Sketch048
  Type = 0
FEATURE [Sketcher::SketchObject] Sketch049
  AttachmentOffset = pos=(0,0,-6) rot=(0,0,1;0rad)
  MapMode = 5
  Placement = pos=(8e-15,8e-15,0) rot=(0.281085,0.678598,0.678598;2.59356rad)
  Support = -> [Pocket004]
  sketch-geometry (6):
    g0: Circle [constr] CenterX=-62.2661 CenterY=127.565 CenterZ=0 NormalX=0 NormalY=0 NormalZ=1 AngleXU=0 Radius=6
    g1: Circle [constr] CenterX=-62.9226 CenterY=103.514 CenterZ=0 NormalX=0 NormalY=0 NormalZ=1 AngleXU=0 Radius=6
    g2: Circle [constr] CenterX=-50.5725 CenterY=76.7215 CenterZ=0 NormalX=0 NormalY=0 NormalZ=1 AngleXU=0 Radius=6
    g3: BSplineCurve PolesCount=3 KnotsCount=2 Degree=2 IsPeriodic=0
    g4: GeomPoint [constr] X=-62.2661 Y=127.565 Z=0
    g5: GeomPoint [constr] X=-50.5725 Y=76.7215 Z=0
  constraints (8):
    c: Radius(g0) = 6
    c: Equal(g0,g1)
    c: Equal(g0,g2)
    c: InternalAlignment(g0,g3)
    c: InternalAlignment(g1,g3)
    c: InternalAlignment(g2,g3)
    c: InternalAlignment(g4,g3)
    c: InternalAlignment(g5,g3)
FEATURE [PartDesign::SubtractivePipe] SubtractivePipe001
  AuxilleryCurvelinear = true
  AuxillerySpineTangent = false
  BaseFeature = -> Pocket004
  Binormal = (0,0,0)
  Mode = 0
  Profile = -> Sketch046
  Spine = -> Sketch049
  SpineTangent = false
  Transformation = 0
  Transition = 0
FEATURE [Sketcher::SketchObject] Sketch050
  ExternalGeometry = -> [SubtractivePipe001]
  MapMode = 5
  Placement = pos=(0,0,0) rot=(1,0,0;1.5708rad)
  Support = -> [XZ_Plane]
  sketch-geometry (15):
    g0: Circle CenterX=21.6267 CenterY=4.32284 CenterZ=0 NormalX=0 NormalY=0 NormalZ=1 AngleXU=0 Radius=1
    g1: Circle CenterX=26.8168 CenterY=4.32284 CenterZ=0 NormalX=0 NormalY=0 NormalZ=1 AngleXU=0 Radius=1
    g2: Circle CenterX=32.0069 CenterY=4.32284 CenterZ=0 NormalX=0 NormalY=0 NormalZ=1 AngleXU=0 Radius=1
    g3: Circle CenterX=37.197 CenterY=4.32284 CenterZ=0 NormalX=0 NormalY=0 NormalZ=1 AngleXU=0 Radius=1
    g4: Circle CenterX=42.3871 CenterY=4.32284 CenterZ=0 NormalX=0 NormalY=0 NormalZ=1 AngleXU=0 Radius=1
    g5: LineSegment [constr] StartX=21.6267 StartY=4.32284 StartZ=0 EndX=26.8168 EndY=4.32284 EndZ=0
    g6: LineSegment [constr] StartX=26.8168 StartY=4.32284 StartZ=0 EndX=32.0069 EndY=4.32284 EndZ=0
    g7: LineSegment [constr] StartX=32.0069 StartY=4.32284 StartZ=0 EndX=37.197 EndY=4.32284 EndZ=0
    g8: LineSegment [constr] StartX=37.197 StartY=4.32284 StartZ=0 EndX=42.3871 EndY=4.32284 EndZ=0
    g9: LineSegment [constr] StartX=16.4366 StartY=6.2 StartZ=0 EndX=16.4366 EndY=1.6 EndZ=0
    g10: LineSegment [constr] StartX=47.5772 StartY=1.6 StartZ=0 EndX=47.5772 EndY=6.2 EndZ=0
    g11: LineSegment [constr] StartX=42.3871 StartY=4.32284 StartZ=0 EndX=47.5772 EndY=4.32284 EndZ=0
    g12: LineSegment [constr] StartX=21.6267 StartY=4.32284 StartZ=0 EndX=16.4366 EndY=4.32284 EndZ=0
    g13: LineSegment [constr] StartX=-47.4403 StartY=1.6 StartZ=0 EndX=-47.4403 EndY=6.2 EndZ=0
    g14: LineSegment [constr] StartX=-16.4112 StartY=6.2 StartZ=0 EndX=-16.4112 EndY=1.6 EndZ=0
  constraints (40):
    c: Radius(g0) = 1
    c: Equal(g0,g1)
    c: Equal(g1,g2)
    c: Equal(g2,g3)
    c: Equal(g3,g4)
    c: Coincident(g5,g0)
    c: Coincident(g5,g1)
    c: Horizontal(g5)
    c: Coincident(g6,g1)
    c: Coincident(g6,g2)
    c: Horizontal(g6)
    c: Coincident(g7,g2)
    c: Coincident(g7,g3)
    c: Coincident(g8,g3)
    c: Coincident(g8,g4)
    c: Horizontal(g8)
    c: Horizontal(g7)
    c: Coincident(g9,g-6)
    c: PointOnObject(g9,g-3)
    c: Vertical(g9)
    c: Coincident(g10,g-3)
    c: PointOnObject(g10,g-6)
    c: Vertical(g10)
    c: Coincident(g11,g4)
    c: PointOnObject(g11,g10)
    c: Coincident(g12,g0)
    c: PointOnObject(g12,g9)
    c: Horizontal(g11)
    c: Horizontal(g12)
    c: Equal(g11,g8)
    c: Equal(g7,g8)
    c: Equal(g7,g6)
    c: Equal(g6,g12)
    c: Equal(g12,g5)
    c: Coincident(g13,g-4)
    c: PointOnObject(g13,g-5)
    c: Vertical(g13)
    c: Coincident(g14,g-5)
    c: PointOnObject(g14,g-4)
    c: Vertical(g14)
FEATURE [PartDesign::Groove] Groove
  Angle = 360
  Axis = (0,-1.035e-13,1)
  Base = (0,0,0)
  BaseFeature = -> SubtractivePipe001
  Profile = -> Sketch050
  ReferenceAxis = -> Sketch050 [V_Axis]
FEATURE [Sketcher::SketchObject] Sketch051
  MapMode = 5
  Placement = pos=(0,0,0) rot=(1,0,0;3.14159rad)
  Support = -> [Groove]
  sketch-geometry (1):
    g0: Circle CenterX=0 CenterY=0 CenterZ=0 NormalX=0 NormalY=0 NormalZ=1 AngleXU=0 Radius=99.9509
  constraints (1):
    c: Coincident(g0,g-1)
FEATURE [PartDesign::Pocket] Pocket005
  BaseFeature = -> Groove
  Length = 0.6
  Length2 = 100
  Profile = -> Sketch051
  Type = 0
FEATURE [PartDesign::Body] Body
  Group = -> [Sketch,Pad,Sketch001,Sketch002,AdditiveLoft,Chamfer,Sketch018,Sketch019,AdditiveLoft001,Sketch021,Sketch022,AdditiveLoft002,Pad017,Sketch026,Sketch027,Pocket,Sketch028,Pocket001,Sketch029,Pocket002,Sketch030,Pocket003,Sketch031,Pad018,Fillet,Fillet001,Sketch032,Pad019,Sketch033,Sketch034,AdditiveLoft003,Sketch035,Sketch036,AdditiveLoft004,Sketch037,Sketch038,AdditiveLoft005,Sketch040,Sketch045,+13 more]
  Origin = -> Origin
  Tip = -> Pocket005
